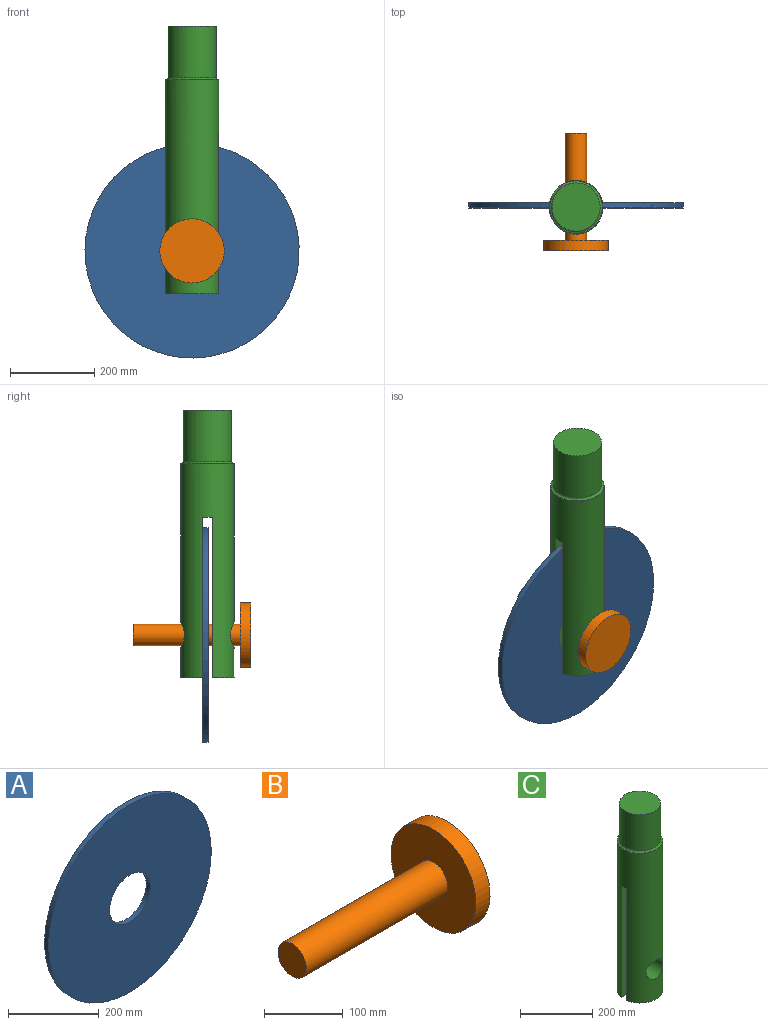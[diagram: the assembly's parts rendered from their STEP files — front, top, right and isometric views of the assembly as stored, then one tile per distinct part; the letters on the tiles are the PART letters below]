
ASSEMBLY  parts=3 mates=4
PART A: 6 faces, bbox 508x12.7x508 mm
  f0: cylinder r=254mm len=508mm, axis (0,1,0), area 20268.3mm2, adj f2,f3,f4
  f1: cylinder r=63.5mm len=127mm, axis (0,1,0), area 5067.1mm2, adj f2,f3
  f2: plane 508x508mm, normal (0,-1,0), area 190015.3mm2, adj f0,f1
  f3: plane 508x508mm, normal (0,1,0), area 190015.3mm2, adj f0,f1
  f4: cylinder r=1.27mm len=127mm, axis (1,0,0), area 1013.4mm2, adj f0,f5
  f5: plane 2.54x2.54mm, normal (1,0,0), area 5.1mm2, adj f4
PART B: 5 faces, bbox 279.4x152.4x152.4 mm
  f0: cylinder r=25.4mm len=254mm, axis (-1,0,0), area 40536.6mm2, adj f1,f4
  f1: plane 50.8x50.8mm, normal (-1,0,0), area 2026.8mm2, adj f0
  f2: plane 152.4x152.4mm, normal (1,0,0), area 18241.5mm2, adj f3
  f3: cylinder r=76.2mm len=152.4mm, axis (-1,0,0), area 12161mm2, adj f2,f4
  f4: plane 152.4x152.4mm, normal (-1,0,0), area 16214.6mm2, adj f0,f3
PART C: 12 faces, bbox 142.5x142.5x635 mm
  f0: plane 125x52.29mm, normal (0,0,-1), area 4917.4mm2, adj f1,f4
  f1: cylinder r=63.5mm len=508mm, axis (0,0,-1), area 178953.2mm2, adj f0,f2,f3,f4,f5,f6,f7,f8
  f2: plane 127x127mm, normal (0,0,1), area 501.6mm2, adj f1,f11
  f3: plane 125x52.29mm, normal (0,0,-1), area 4917.4mm2, adj f1,f5
  f4: plane 381x125mm, normal (0,-1,0), area 44459.9mm2, adj f0,f1,f6,f8
  f5: plane 381x125mm, normal (0,1,0), area 44459.9mm2, adj f1,f3,f6,f7
  f6: plane 127x22.42mm, normal (0,0,-1), area 2832.9mm2, adj f1,f4,f5
  f7: cylinder r=31.75mm len=63.5mm, axis (0,1,0), area 9597.2mm2, adj f1,f5
  f8: cylinder r=31.75mm len=63.5mm, axis (0,-1,0), area 9597.2mm2, adj f1,f4
  f9: cylinder r=57.15mm len=121.92mm, axis (0,0,-1), area 43779.5mm2, adj f10,f11
  f10: plane 114.3x114.3mm, normal (0,0,1), area 10260.8mm2, adj f9
  f11: torus R=62.23mm, axis (0,0,1), area 2957.9mm2, adj f2,f9
PLACE A rot(axis=(0,-1,0),45.1deg) t=(-209.62,66.48,48.54)mm
PLACE B rot(axis=(0.08,-0.08,-0.99),90.3deg) t=(-209.62,231.58,48.54)mm
PLACE C t=(-209.62,55.27,-53.06)mm fixed
MATE parallel A.f0 <-> B.f0  axis (0,-1,0) through (-209.62,53.78,48.54)mm
MATE cylindrical C.f7 <-> A.f0  axis (0,-1,0) through (-209.62,92.83,48.54)mm
MATE cylindrical B.f0 <-> C.f7  axis (0,1,0) through (-209.62,104.58,48.54)mm
MATE planar A.f0 <-> C.f4  axis (0,1,0) through (-209.62,66.48,48.54)mm
